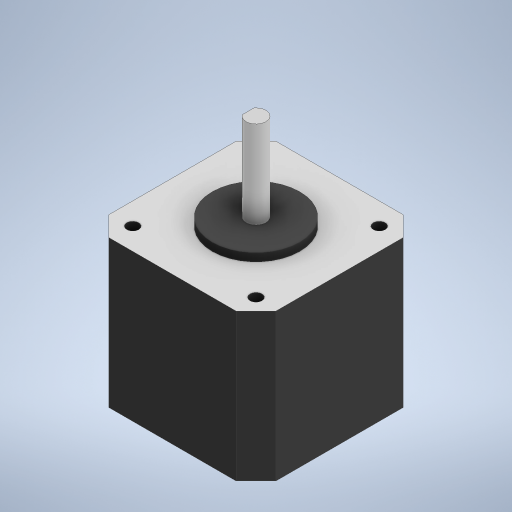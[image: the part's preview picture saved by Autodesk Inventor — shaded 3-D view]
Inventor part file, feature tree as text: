
AUTODESK INVENTOR PART (.ipt)
format: ipt  version: 2023 (Build 270158000, 158)  size: 275,456 bytes
history: native  units: mm
features: extrude x5, sketch x5, other x1
ambient origin geometry x8: Origin, YZ Plane, XZ Plane, XY Plane, X Axis, Y Axis, Z Axis, Center Point
bodies: Body1 (feature_tree)
feature tree (11):
  other  "솔리드1"
  extrude  "돌출1"  Depth=42.0mm
  extrude  "돌출2"  Depth=42.0mm
  extrude  "돌출3"  Depth=5.0mm
  extrude  "돌출4"  Depth=5.0mm
  extrude  "돌출5"  Depth=5.0mm
  sketch  "스케치1"
  sketch  "스케치2"
  sketch  "스케치3"
  sketch  "스케치4"
  sketch  "스케치5"
